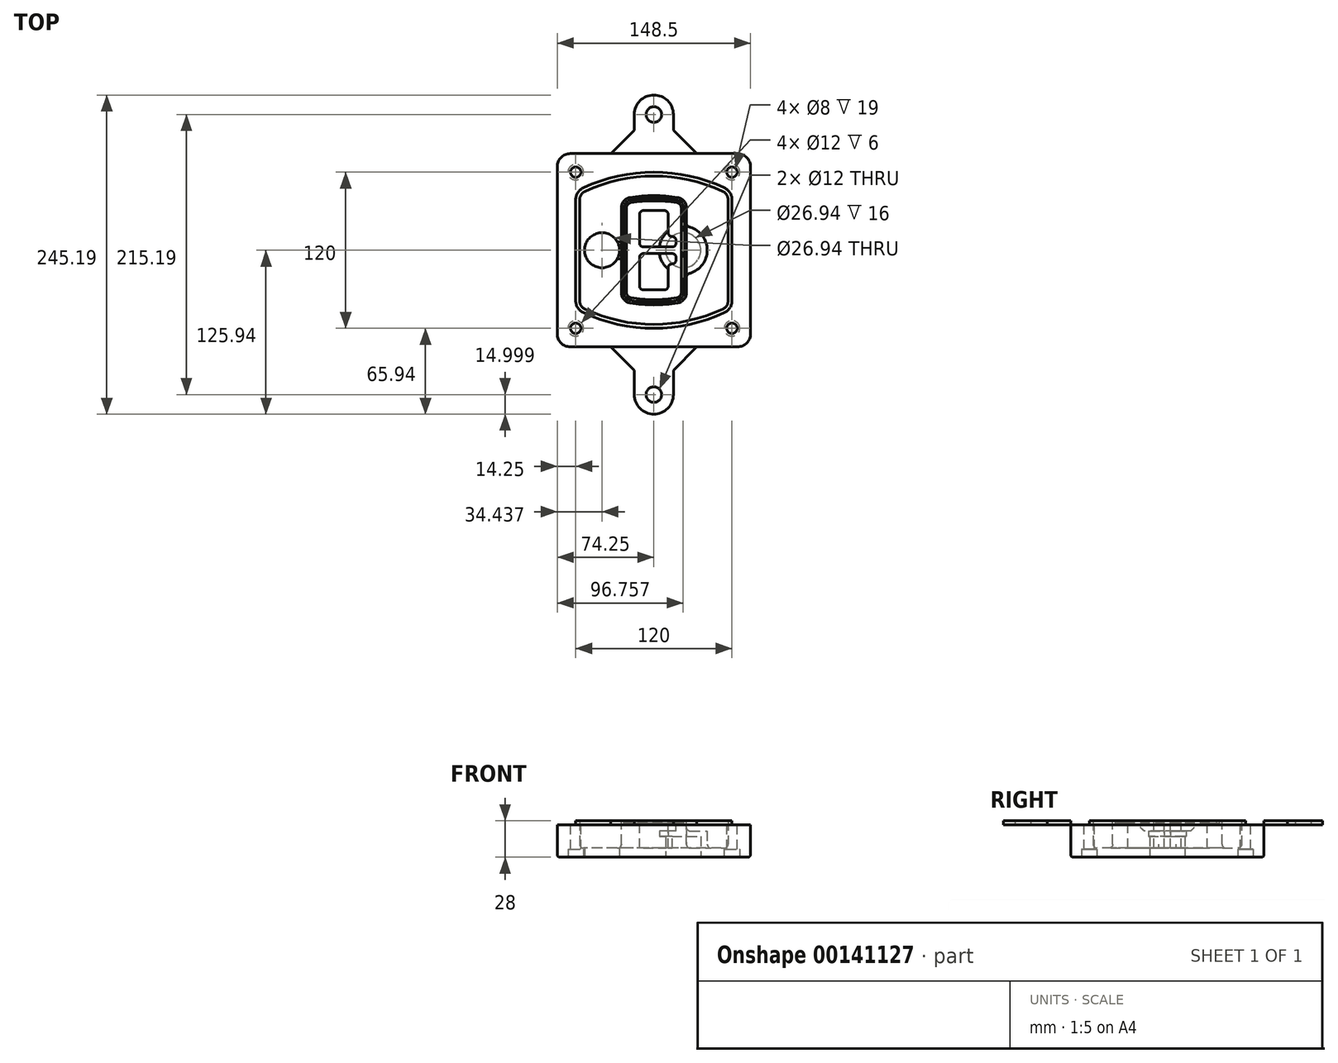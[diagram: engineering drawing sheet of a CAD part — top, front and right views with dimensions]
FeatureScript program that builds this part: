
annotation { "Feature Type Name" : "Feature", "Feature Type Description" : "" }
export const myFeature = defineFeature(function(context is Context, id is Id, definition is map)
    precondition{}
    {
        {
            var Q0;
            Q0=qCreatedBy(makeId("Top.planeOp"),FACE);
            var sketch = newSketch(context, id + "F0", { "sketchPlane" : qUnion([Q0])});
            skPoint(sketch, "E0.rect.middle", {"position": v(0, 0) * mm});
            skLineSegment(sketch, "E1.bottom", {"start": v(-64.25, -74.25) * mm, "end": v(64.25, -74.25) * mm});
            skLineSegment(sketch, "E1.top", {"start": v(-64.25, 74.25) * mm, "end": v(64.25, 74.25) * mm});
            skLineSegment(sketch, "E1.left", {"start": v(-74.25, -64.25) * mm, "end": v(-74.25, 64.25) * mm});
            skLineSegment(sketch, "E1.right", {"start": v(74.25, -64.25) * mm, "end": v(74.25, 64.25) * mm});
            skLineSegment(sketch, "E2", {"start": v(-74.25, 74.25) * mm, "end": v(74.25, -74.25) * mm, "construction": true});
            skLineSegment(sketch, "E3", {"start": v(74.25, 74.25) * mm, "end": v(-74.25, -74.25) * mm, "construction": true});
            skCircle(sketch, "E4", {"center": v(-60, 60) * mm, "radius": 4 * mm});
            skCircle(sketch, "E5", {"center": v(60, 60) * mm, "radius": 4 * mm});
            skCircle(sketch, "E6", {"center": v(60, -60) * mm, "radius": 4 * mm});
            skCircle(sketch, "E7", {"center": v(-60, -60) * mm, "radius": 4 * mm});
            skLineSegment(sketch, "E8", {"start": v(-60, 60) * mm, "end": v(60, 60) * mm, "construction": true});
            skLineSegment(sketch, "E9", {"start": v(60, 60) * mm, "end": v(60, -60) * mm, "construction": true});
            skLineSegment(sketch, "E10", {"start": v(60, -60) * mm, "end": v(-60, -60) * mm, "construction": true});
            skLineSegment(sketch, "E11", {"start": v(-60, -60) * mm, "end": v(-60, 60) * mm, "construction": true});
            skLineSegment(sketch, "E12", {"start": v(-60, 38.83) * mm, "end": v(-60, -38.83) * mm});
            skLineSegment(sketch, "E13", {"start": v(60, 38.83) * mm, "end": v(60, -38.83) * mm});
            skArc(sketch, "E14", {"start": v(54.26, 47.88) * mm, "mid": v(0, 60) * mm, "end": v(-54.26, 47.88) * mm});
            skArc(sketch, "E15", {"start": v(-54.26, -47.88) * mm, "mid": v(0, -60) * mm, "end": v(54.26, -47.88) * mm});
            skLineSegment(sketch, "E16", {"start": v(-60, 0) * mm, "end": v(60, 0) * mm, "construction": true});
            skPoint(sketch, "E17.visualSharp", {"position": v(-60, -45) * mm});
            skArc(sketch, "E17.filletArc", {"start": v(-60, -38.83) * mm, "mid": v(-58.44, -44.2) * mm, "end": v(-54.26, -47.88) * mm});
            skPoint(sketch, "E18.visualSharp", {"position": v(-60, 45) * mm});
            skArc(sketch, "E18.filletArc", {"start": v(-54.26, 47.88) * mm, "mid": v(-58.44, 44.2) * mm, "end": v(-60, 38.83) * mm});
            skPoint(sketch, "E19.visualSharp", {"position": v(60, 45) * mm});
            skArc(sketch, "E19.filletArc", {"start": v(60, 38.83) * mm, "mid": v(58.44, 44.2) * mm, "end": v(54.26, 47.88) * mm});
            skPoint(sketch, "E20.visualSharp", {"position": v(60, -45) * mm});
            skArc(sketch, "E20.filletArc", {"start": v(54.26, -47.88) * mm, "mid": v(58.44, -44.2) * mm, "end": v(60, -38.83) * mm});
            skPoint(sketch, "E21.visualSharp", {"position": v(-74.25, 74.25) * mm});
            skArc(sketch, "E21.filletArc", {"start": v(-64.25, 74.25) * mm, "mid": v(-71.32, 71.32) * mm, "end": v(-74.25, 64.25) * mm});
            skPoint(sketch, "E22.visualSharp", {"position": v(74.25, 74.25) * mm});
            skArc(sketch, "E22.filletArc", {"start": v(74.25, 64.25) * mm, "mid": v(71.32, 71.32) * mm, "end": v(64.25, 74.25) * mm});
            skPoint(sketch, "E23.visualSharp", {"position": v(74.25, -74.25) * mm});
            skArc(sketch, "E23.filletArc", {"start": v(64.25, -74.25) * mm, "mid": v(71.32, -71.32) * mm, "end": v(74.25, -64.25) * mm});
            skPoint(sketch, "E24.visualSharp", {"position": v(-74.25, -74.25) * mm});
            skArc(sketch, "E24.filletArc", {"start": v(-74.25, -64.25) * mm, "mid": v(-71.32, -71.32) * mm, "end": v(-64.25, -74.25) * mm});
            skArc(sketch, "E25.0", {"start": v(57, 38.83) * mm, "mid": v(55.9, 42.58) * mm, "end": v(52.98, 45.17) * mm});
            skLineSegment(sketch, "E25.1", {"start": v(57, 38.83) * mm, "end": v(57, -38.83) * mm});
            skArc(sketch, "E25.2", {"start": v(52.98, -45.17) * mm, "mid": v(55.9, -42.58) * mm, "end": v(57, -38.83) * mm});
            skArc(sketch, "E25.3", {"start": v(-52.98, -45.17) * mm, "mid": v(0, -57) * mm, "end": v(52.98, -45.17) * mm});
            skArc(sketch, "E25.4", {"start": v(-57, -38.83) * mm, "mid": v(-55.9, -42.58) * mm, "end": v(-52.98, -45.17) * mm});
            skArc(sketch, "E25.5", {"start": v(52.98, 45.17) * mm, "mid": v(0, 57) * mm, "end": v(-52.98, 45.17) * mm});
            skLineSegment(sketch, "E25.6", {"start": v(-57, 38.83) * mm, "end": v(-57, -38.83) * mm});
            skArc(sketch, "E25.7", {"start": v(-52.98, 45.17) * mm, "mid": v(-55.9, 42.58) * mm, "end": v(-57, 38.83) * mm});
            skArc(sketch, "E26.0", {"start": v(-55.96, 51.5) * mm, "mid": v(-61.82, 46.33) * mm, "end": v(-64, 38.83) * mm});
            skArc(sketch, "E26.1", {"start": v(55.96, 51.5) * mm, "mid": v(0, 64) * mm, "end": v(-55.96, 51.5) * mm});
            skArc(sketch, "E26.2", {"start": v(64, 38.83) * mm, "mid": v(61.82, 46.33) * mm, "end": v(55.96, 51.5) * mm});
            skLineSegment(sketch, "E26.3", {"start": v(64, 38.83) * mm, "end": v(64, -38.83) * mm});
            skArc(sketch, "E26.4", {"start": v(55.96, -51.5) * mm, "mid": v(61.82, -46.33) * mm, "end": v(64, -38.83) * mm});
            skLineSegment(sketch, "E26.5", {"start": v(-64, 38.83) * mm, "end": v(-64, -38.83) * mm});
            skArc(sketch, "E26.6", {"start": v(-55.96, -51.5) * mm, "mid": v(0, -64) * mm, "end": v(55.96, -51.5) * mm});
            skArc(sketch, "E26.7", {"start": v(-64, -38.83) * mm, "mid": v(-61.82, -46.33) * mm, "end": v(-55.96, -51.5) * mm});
            skSolve(sketch);
        }
        {
            var Q0;
            Q0=makeQuery(id+"F0.imprint","IMPRINT",FACE,{"disambiguationData":[TD([[makeQuery(id+"F0.imprint","IMPRINT",EDGE,{"derivedFrom":sQuery(id+"F0.wireOp",EDGE,"E1.bottom")}),1.0]])]});
            var Q1;
            Q1=makeQuery(id+"F0.imprint","IMPRINT",FACE,{"disambiguationData":[TD([[makeQuery(id+"F0.imprint","IMPRINT",EDGE,{"derivedFrom":sQuery(id+"F0.wireOp",EDGE,"E12")}),1.0]])]});
            var Q2;
            Q2=makeQuery(id+"F0.imprint","IMPRINT",FACE,{"disambiguationData":[TD([[makeQuery(id+"F0.imprint","IMPRINT",EDGE,{"derivedFrom":sQuery(id+"F0.wireOp",EDGE,"E25.0")}),1.0]])]});
            var Q3;
            Q3=makeQuery(id+"F0.imprint","IMPRINT",FACE,{"disambiguationData":[TD([[makeQuery(id+"F0.imprint","IMPRINT",EDGE,{"derivedFrom":sQuery(id+"F0.wireOp",EDGE,"E12")}),-1.0]])]});
            extrude(context, id + "F1", {"entities" : qUnion([Q0, Q1, Q2, Q3]), "oppositeDirection" : true, "depth" : 25 * mm});
        }
        {
            var Q0;
            Q0=makeQuery(id+"F0.imprint","IMPRINT",FACE,{"disambiguationData":[TD([[makeQuery(id+"F0.imprint","IMPRINT",EDGE,{"derivedFrom":sQuery(id+"F0.wireOp",EDGE,"E12")}),1.0]])]});
            extrude(context, id + "F2", {"entities" : qUnion([Q0]), "operationType" : NewBodyOperationType.ADD, "depth" : 3 * mm});
        }
        {
            var Q0;
            Q0=makeQuery(id+"F0.imprint","IMPRINT",FACE,{"disambiguationData":[TD([[makeQuery(id+"F0.imprint","IMPRINT",EDGE,{"derivedFrom":sQuery(id+"F0.wireOp",EDGE,"E25.0")}),1.0]])]});
            extrude(context, id + "F3", {"entities" : qUnion([Q0]), "operationType" : NewBodyOperationType.REMOVE, "oppositeDirection" : true, "depth" : 18 * mm});
        }
        {
            var Q0;
            Q0=makeQuery(id+"F2.opExtrude","CAP_FACE",FACE,{"disambiguationData":[OSD([sQuery(id+"F0.wireOp",EDGE,"E12"),sQuery(id+"F0.wireOp",EDGE,"E13"),sQuery(id+"F0.wireOp",EDGE,"E14"),sQuery(id+"F0.wireOp",EDGE,"E15"),sQuery(id+"F0.wireOp",EDGE,"E17.filletArc"),sQuery(id+"F0.wireOp",EDGE,"E18.filletArc"),sQuery(id+"F0.wireOp",EDGE,"E19.filletArc"),sQuery(id+"F0.wireOp",EDGE,"E20.filletArc"),sQuery(id+"F0.wireOp",EDGE,"E25.0"),sQuery(id+"F0.wireOp",EDGE,"E25.1"),sQuery(id+"F0.wireOp",EDGE,"E25.2"),sQuery(id+"F0.wireOp",EDGE,"E25.3"),sQuery(id+"F0.wireOp",EDGE,"E25.4"),sQuery(id+"F0.wireOp",EDGE,"E25.5"),sQuery(id+"F0.wireOp",EDGE,"E25.6"),sQuery(id+"F0.wireOp",EDGE,"E25.7")])],"isStart":false});
            var sketch = newSketch(context, id + "F4", { "sketchPlane" : qUnion([Q0])});
            skArc(sketch, "E27.0", {"start": v(-18.34, -40.45) * mm, "mid": v(0, -42) * mm, "end": v(18.34, -40.45) * mm});
            skArc(sketch, "E28.0", {"start": v(18.34, 40.45) * mm, "mid": v(0, 42) * mm, "end": v(-18.34, 40.45) * mm});
            skLineSegment(sketch, "E29", {"start": v(-25, 32.57) * mm, "end": v(-25, -32.57) * mm});
            skLineSegment(sketch, "E30", {"start": v(25, 32.57) * mm, "end": v(25, -32.57) * mm});
            skLineSegment(sketch, "E31", {"start": v(-25, 39.1) * mm, "end": v(25, 39.1) * mm, "construction": true});
            skLineSegment(sketch, "E32", {"start": v(-25, -39.1) * mm, "end": v(25, -39.1) * mm, "construction": true});
            skPoint(sketch, "E33.visualSharp", {"position": v(-25, 39.1) * mm});
            skArc(sketch, "E33.filletArc", {"start": v(-18.34, 40.45) * mm, "mid": v(-23.11, 37.73) * mm, "end": v(-25, 32.57) * mm});
            skPoint(sketch, "E34.visualSharp", {"position": v(25, 39.1) * mm});
            skArc(sketch, "E34.filletArc", {"start": v(25, 32.57) * mm, "mid": v(23.11, 37.73) * mm, "end": v(18.34, 40.45) * mm});
            skPoint(sketch, "E35.visualSharp", {"position": v(25, -39.1) * mm});
            skArc(sketch, "E35.filletArc", {"start": v(18.34, -40.45) * mm, "mid": v(23.11, -37.73) * mm, "end": v(25, -32.57) * mm});
            skPoint(sketch, "E36.visualSharp", {"position": v(-25, -39.1) * mm});
            skArc(sketch, "E36.filletArc", {"start": v(-25, -32.57) * mm, "mid": v(-23.11, -37.73) * mm, "end": v(-18.34, -40.45) * mm});
            skArc(sketch, "E37.0", {"start": v(52.98, 45.17) * mm, "mid": v(0, 57) * mm, "end": v(-52.98, 45.17) * mm});
            skArc(sketch, "E37.1", {"start": v(-52.98, 45.17) * mm, "mid": v(-55.9, 42.58) * mm, "end": v(-57, 38.83) * mm});
            skLineSegment(sketch, "E37.2", {"start": v(-57, 38.83) * mm, "end": v(-57, -38.83) * mm});
            skArc(sketch, "E37.3", {"start": v(-57, -38.83) * mm, "mid": v(-55.9, -42.58) * mm, "end": v(-52.98, -45.17) * mm});
            skArc(sketch, "E37.4", {"start": v(-52.98, -45.17) * mm, "mid": v(0, -57) * mm, "end": v(52.98, -45.17) * mm});
            skArc(sketch, "E37.5", {"start": v(52.98, -45.17) * mm, "mid": v(55.9, -42.58) * mm, "end": v(57, -38.83) * mm});
            skLineSegment(sketch, "E37.6", {"start": v(57, 38.83) * mm, "end": v(57, -38.83) * mm});
            skArc(sketch, "E37.7", {"start": v(57, 38.83) * mm, "mid": v(55.9, 42.58) * mm, "end": v(52.98, 45.17) * mm});
            skLineSegment(sketch, "E38.0", {"start": v(23, 32.57) * mm, "end": v(23, -32.57) * mm});
            skArc(sketch, "E38.1", {"start": v(18, -38.48) * mm, "mid": v(21.58, -36.44) * mm, "end": v(23, -32.57) * mm});
            skArc(sketch, "E38.2", {"start": v(-18, -38.48) * mm, "mid": v(0, -40) * mm, "end": v(18, -38.48) * mm});
            skArc(sketch, "E38.3", {"start": v(-23, -32.57) * mm, "mid": v(-21.58, -36.44) * mm, "end": v(-18, -38.48) * mm});
            skLineSegment(sketch, "E38.4", {"start": v(-23, 32.57) * mm, "end": v(-23, -32.57) * mm});
            skArc(sketch, "E38.5", {"start": v(23, 32.57) * mm, "mid": v(21.58, 36.44) * mm, "end": v(18, 38.48) * mm});
            skArc(sketch, "E38.6", {"start": v(-18, 38.48) * mm, "mid": v(-21.58, 36.44) * mm, "end": v(-23, 32.57) * mm});
            skArc(sketch, "E38.7", {"start": v(18, 38.48) * mm, "mid": v(0, 40) * mm, "end": v(-18, 38.48) * mm});
            skArc(sketch, "E39.0", {"start": v(21, 32.57) * mm, "mid": v(20.06, 35.15) * mm, "end": v(17.67, 36.5) * mm});
            skLineSegment(sketch, "E39.1", {"start": v(21, 32.57) * mm, "end": v(21, -32.57) * mm});
            skArc(sketch, "E39.2", {"start": v(17.67, -36.5) * mm, "mid": v(20.06, -35.15) * mm, "end": v(21, -32.57) * mm});
            skArc(sketch, "E39.3", {"start": v(-17.67, -36.5) * mm, "mid": v(0, -38) * mm, "end": v(17.67, -36.5) * mm});
            skArc(sketch, "E39.4", {"start": v(-21, -32.57) * mm, "mid": v(-20.06, -35.15) * mm, "end": v(-17.67, -36.5) * mm});
            skArc(sketch, "E39.5", {"start": v(17.67, 36.5) * mm, "mid": v(0, 38) * mm, "end": v(-17.67, 36.5) * mm});
            skLineSegment(sketch, "E39.6", {"start": v(-21, 32.57) * mm, "end": v(-21, -32.57) * mm});
            skArc(sketch, "E39.7", {"start": v(-17.67, 36.5) * mm, "mid": v(-20.06, 35.15) * mm, "end": v(-21, 32.57) * mm});
            skLineSegment(sketch, "E40", {"start": v(-25, 0) * mm, "end": v(25, 0) * mm, "construction": true});
            skLineSegment(sketch, "E41", {"start": v(-11, 5.5) * mm, "end": v(-11, 27.5) * mm});
            skLineSegment(sketch, "E42", {"start": v(-8, 30.5) * mm, "end": v(8, 30.5) * mm});
            skLineSegment(sketch, "E43", {"start": v(11, 27.5) * mm, "end": v(11, 13.5) * mm});
            skLineSegment(sketch, "E44", {"start": v(14, 10.5) * mm, "end": v(14, 10.5) * mm});
            skLineSegment(sketch, "E45", {"start": v(17, 7.5) * mm, "end": v(17, 5.5) * mm});
            skLineSegment(sketch, "E46", {"start": v(14, 2.5) * mm, "end": v(-8, 2.5) * mm});
            skPoint(sketch, "E47.visualSharp", {"position": v(-11, 30.5) * mm});
            skArc(sketch, "E47.filletArc", {"start": v(-8, 30.5) * mm, "mid": v(-10.12, 29.62) * mm, "end": v(-11, 27.5) * mm});
            skPoint(sketch, "E48.visualSharp", {"position": v(11, 30.5) * mm});
            skArc(sketch, "E48.filletArc", {"start": v(11, 27.5) * mm, "mid": v(10.12, 29.62) * mm, "end": v(8, 30.5) * mm});
            skPoint(sketch, "E49.visualSharp", {"position": v(11, 10.5) * mm});
            skArc(sketch, "E49.filletArc", {"start": v(11, 13.5) * mm, "mid": v(11.88, 11.38) * mm, "end": v(14, 10.5) * mm});
            skPoint(sketch, "E50.visualSharp", {"position": v(17, 10.5) * mm});
            skArc(sketch, "E50.filletArc", {"start": v(17, 7.5) * mm, "mid": v(16.12, 9.62) * mm, "end": v(14, 10.5) * mm});
            skPoint(sketch, "E51.visualSharp", {"position": v(17, 2.5) * mm});
            skArc(sketch, "E51.filletArc", {"start": v(14, 2.5) * mm, "mid": v(16.12, 3.38) * mm, "end": v(17, 5.5) * mm});
            skPoint(sketch, "E52.visualSharp", {"position": v(-11, 2.5) * mm});
            skArc(sketch, "E52.filletArc", {"start": v(-11, 5.5) * mm, "mid": v(-10.12, 3.38) * mm, "end": v(-8, 2.5) * mm});
            skLineSegment(sketch, "E53.0.MirrorCS", {"start": v(14, -2.5) * mm, "end": v(-8, -2.5) * mm});
            skArc(sketch, "E54.0.MirrorCS", {"start": v(-11, -5.5) * mm, "mid": v(-10.12, -3.38) * mm, "end": v(-8, -2.5) * mm});
            skLineSegment(sketch, "E55.0.MirrorCS", {"start": v(-11, -5.5) * mm, "end": v(-11, -27.5) * mm});
            skArc(sketch, "E56.0.MirrorCS", {"start": v(-8, -30.5) * mm, "mid": v(-10.12, -29.62) * mm, "end": v(-11, -27.5) * mm});
            skLineSegment(sketch, "E57.0.MirrorCS", {"start": v(-8, -30.5) * mm, "end": v(8, -30.5) * mm});
            skArc(sketch, "E58.0.MirrorCS", {"start": v(11, -27.5) * mm, "mid": v(10.12, -29.62) * mm, "end": v(8, -30.5) * mm});
            skLineSegment(sketch, "E59.0.MirrorCS", {"start": v(11, -27.5) * mm, "end": v(11, -13.5) * mm});
            skArc(sketch, "E60.0.MirrorCS", {"start": v(11, -13.5) * mm, "mid": v(11.88, -11.38) * mm, "end": v(14, -10.5) * mm});
            skArc(sketch, "E61.0.MirrorCS", {"start": v(17, -7.5) * mm, "mid": v(16.12, -9.62) * mm, "end": v(14, -10.5) * mm});
            skLineSegment(sketch, "E62.0.MirrorCS", {"start": v(17, -7.5) * mm, "end": v(17, -5.5) * mm});
            skArc(sketch, "E63.0.MirrorCS", {"start": v(14, -2.5) * mm, "mid": v(16.12, -3.38) * mm, "end": v(17, -5.5) * mm});
            skSolve(sketch);
        }
        {
            var Q0;
            Q0=makeQuery(id+"F4.imprint","IMPRINT",FACE,{"disambiguationData":[TD([[makeQuery(id+"F4.imprint","IMPRINT",EDGE,{"derivedFrom":sQuery(id+"F4.wireOp",EDGE,"E27.0")}),1.0]])]});
            var Q1;
            Q1=makeQuery(id+"F4.imprint","IMPRINT",FACE,{"disambiguationData":[TD([[makeQuery(id+"F4.imprint","IMPRINT",EDGE,{"derivedFrom":sQuery(id+"F4.wireOp",EDGE,"E38.0")}),-1.0]])]});
            var Q2;
            Q2=makeQuery(id+"F4.imprint","IMPRINT",FACE,{"disambiguationData":[TD([[makeQuery(id+"F4.imprint","IMPRINT",EDGE,{"derivedFrom":sQuery(id+"F4.wireOp",EDGE,"E39.0")}),1.0]])]});
            extrude(context, id + "F5", {"entities" : qUnion([Q0, Q1, Q2]), "operationType" : NewBodyOperationType.ADD, "endBound" : BoundingType.UP_TO_NEXT, "oppositeDirection" : true, "depth" : 25 * mm});
        }
        {
            var Q0;
            Q0=makeQuery(id+"F4.imprint","IMPRINT",FACE,{"disambiguationData":[TD([[makeQuery(id+"F4.imprint","IMPRINT",EDGE,{"derivedFrom":sQuery(id+"F4.wireOp",EDGE,"E38.0")}),-1.0]])]});
            extrude(context, id + "F6", {"entities" : qUnion([Q0]), "operationType" : NewBodyOperationType.REMOVE, "oppositeDirection" : true, "depth" : 2 * mm});
        }
        {
            var Q0;
            Q0=makeQuery(id+"F1.opExtrude","CAP_FACE",FACE,{"disambiguationData":[OSD([sQuery(id+"F0.wireOp",EDGE,"E1.bottom"),sQuery(id+"F0.wireOp",EDGE,"E1.top"),sQuery(id+"F0.wireOp",EDGE,"E1.left"),sQuery(id+"F0.wireOp",EDGE,"E1.right"),sQuery(id+"F0.wireOp",EDGE,"E4"),sQuery(id+"F0.wireOp",EDGE,"E5"),sQuery(id+"F0.wireOp",EDGE,"E6"),sQuery(id+"F0.wireOp",EDGE,"E7"),sQuery(id+"F0.wireOp",EDGE,"E21.filletArc"),sQuery(id+"F0.wireOp",EDGE,"E22.filletArc"),sQuery(id+"F0.wireOp",EDGE,"E23.filletArc"),sQuery(id+"F0.wireOp",EDGE,"E24.filletArc")])],"isStart":false});
            var sketch = newSketch(context, id + "F7", { "sketchPlane" : qUnion([Q0])});
            skCircle(sketch, "E64", {"center": v(22.5, 0) * mm, "radius": 13.47 * mm});
            skCircle(sketch, "E65", {"center": v(-39.81, 0) * mm, "radius": 13.47 * mm});
            skLineSegment(sketch, "E66", {"start": v(74.25, 0) * mm, "end": v(-74.25, 0) * mm});
            skCircle(sketch, "E67", {"center": v(22.5, 0) * mm, "radius": 18.47 * mm});
            skCircle(sketch, "E68", {"center": v(60, -60) * mm, "radius": 6 * mm});
            skCircle(sketch, "E69", {"center": v(-60, -60) * mm, "radius": 6 * mm});
            skCircle(sketch, "E70", {"center": v(-60, 60) * mm, "radius": 6 * mm});
            skCircle(sketch, "E71", {"center": v(60, 60) * mm, "radius": 6 * mm});
            skSolve(sketch);
        }
        {
            var Q0;
            {var subQ1=sQuery(id+"F7.wireOp",EDGE,"E66");var subQ4=sQuery(id+"F7.wireOp",EDGE,"E64");var subQ6=makeQuery(id+"F7.imprint","INTERSECT",VERTEX,{"disambiguationData":[OD(0.0)],"derivedFrom":[subQ4,subQ1]});Q0=makeQuery(id+"F7.imprint","IMPRINT",FACE,{"disambiguationData":[TD([[makeQuery(id+"F7.imprint","IMPRINT",EDGE,{"disambiguationData":[TD([[subQ6,-1.0]])],"derivedFrom":subQ4}),-1.0]])]});}
            var Q1;
            {var subQ0=sQuery(id+"F7.wireOp",EDGE,"E66");var subQ1=sQuery(id+"F7.wireOp",EDGE,"E64");var subQ3=makeQuery(id+"F7.imprint","INTERSECT",VERTEX,{"disambiguationData":[OD(0.0)],"derivedFrom":[subQ1,subQ0]});Q1=makeQuery(id+"F7.imprint","IMPRINT",FACE,{"disambiguationData":[TD([[makeQuery(id+"F7.imprint","IMPRINT",EDGE,{"disambiguationData":[TD([[subQ3,-1.0]])],"derivedFrom":subQ1}),1.0]])]});}
            var Q2;
            {var subQ0=sQuery(id+"F7.wireOp",EDGE,"E66");var subQ1=sQuery(id+"F7.wireOp",EDGE,"E64");var subQ3=makeQuery(id+"F7.imprint","INTERSECT",VERTEX,{"disambiguationData":[OD(0.0)],"derivedFrom":[subQ1,subQ0]});Q2=makeQuery(id+"F7.imprint","IMPRINT",FACE,{"disambiguationData":[TD([[makeQuery(id+"F7.imprint","IMPRINT",EDGE,{"disambiguationData":[TD([[subQ3,1.0]])],"derivedFrom":subQ1}),1.0]])]});}
            var Q3;
            {var subQ1=sQuery(id+"F7.wireOp",EDGE,"E66");var subQ4=sQuery(id+"F7.wireOp",EDGE,"E64");var subQ6=makeQuery(id+"F7.imprint","INTERSECT",VERTEX,{"disambiguationData":[OD(0.0)],"derivedFrom":[subQ4,subQ1]});Q3=makeQuery(id+"F7.imprint","IMPRINT",FACE,{"disambiguationData":[TD([[makeQuery(id+"F7.imprint","IMPRINT",EDGE,{"disambiguationData":[TD([[subQ6,1.0]])],"derivedFrom":subQ4}),-1.0]])]});}
            extrude(context, id + "F8", {"entities" : qUnion([Q0, Q1, Q2, Q3]), "operationType" : NewBodyOperationType.ADD, "oppositeDirection" : true, "depth" : 20 * mm});
        }
        {
            var Q0;
            {var subQ0=sQuery(id+"F7.wireOp",EDGE,"E66");var subQ1=sQuery(id+"F7.wireOp",EDGE,"E64");var subQ3=makeQuery(id+"F7.imprint","INTERSECT",VERTEX,{"disambiguationData":[OD(0.0)],"derivedFrom":[subQ1,subQ0]});Q0=makeQuery(id+"F7.imprint","IMPRINT",FACE,{"disambiguationData":[TD([[makeQuery(id+"F7.imprint","IMPRINT",EDGE,{"disambiguationData":[TD([[subQ3,-1.0]])],"derivedFrom":subQ1}),1.0]])]});}
            var Q1;
            {var subQ0=sQuery(id+"F7.wireOp",EDGE,"E66");var subQ1=sQuery(id+"F7.wireOp",EDGE,"E64");var subQ3=makeQuery(id+"F7.imprint","INTERSECT",VERTEX,{"disambiguationData":[OD(0.0)],"derivedFrom":[subQ1,subQ0]});Q1=makeQuery(id+"F7.imprint","IMPRINT",FACE,{"disambiguationData":[TD([[makeQuery(id+"F7.imprint","IMPRINT",EDGE,{"disambiguationData":[TD([[subQ3,1.0]])],"derivedFrom":subQ1}),1.0]])]});}
            extrude(context, id + "F9", {"entities" : qUnion([Q0, Q1]), "operationType" : NewBodyOperationType.REMOVE, "oppositeDirection" : true, "depth" : 16 * mm});
        }
        {
            var Q0;
            {var subQ0=sQuery(id+"F7.wireOp",EDGE,"E66");var subQ1=sQuery(id+"F7.wireOp",EDGE,"E65");var subQ3=makeQuery(id+"F7.imprint","INTERSECT",VERTEX,{"disambiguationData":[OD(0.0)],"derivedFrom":[subQ1,subQ0]});Q0=makeQuery(id+"F7.imprint","IMPRINT",FACE,{"disambiguationData":[TD([[makeQuery(id+"F7.imprint","IMPRINT",EDGE,{"disambiguationData":[TD([[subQ3,-1.0]])],"derivedFrom":subQ1}),1.0]])]});}
            var Q1;
            {var subQ0=sQuery(id+"F7.wireOp",EDGE,"E66");var subQ1=sQuery(id+"F7.wireOp",EDGE,"E65");var subQ3=makeQuery(id+"F7.imprint","INTERSECT",VERTEX,{"disambiguationData":[OD(0.0)],"derivedFrom":[subQ1,subQ0]});Q1=makeQuery(id+"F7.imprint","IMPRINT",FACE,{"disambiguationData":[TD([[makeQuery(id+"F7.imprint","IMPRINT",EDGE,{"disambiguationData":[TD([[subQ3,1.0]])],"derivedFrom":subQ1}),1.0]])]});}
            extrude(context, id + "F10", {"entities" : qUnion([Q0, Q1]), "operationType" : NewBodyOperationType.REMOVE, "oppositeDirection" : true, "depth" : 25 * mm});
        }
        {
            var Q0;
            Q0=makeQuery(id+"F7.imprint","IMPRINT",FACE,{"disambiguationData":[TD([[makeQuery(id+"F7.imprint","IMPRINT",EDGE,{"derivedFrom":sQuery(id+"F7.wireOp",EDGE,"E68")}),1.0]])]});
            var Q1;
            Q1=makeQuery(id+"F7.imprint","IMPRINT",FACE,{"disambiguationData":[TD([[makeQuery(id+"F7.imprint","IMPRINT",EDGE,{"derivedFrom":makeQuery(id+"F1.opExtrude","CAP_EDGE",EDGE,{"disambiguationData":[OSD([sQuery(id+"F0.wireOp",EDGE,"E5")])],"isStart":false})}),-1.0]])]});
            var Q2;
            Q2=makeQuery(id+"F7.imprint","IMPRINT",FACE,{"disambiguationData":[TD([[makeQuery(id+"F7.imprint","IMPRINT",EDGE,{"derivedFrom":sQuery(id+"F7.wireOp",EDGE,"E69")}),1.0]])]});
            var Q3;
            Q3=makeQuery(id+"F7.imprint","IMPRINT",FACE,{"disambiguationData":[TD([[makeQuery(id+"F7.imprint","IMPRINT",EDGE,{"derivedFrom":makeQuery(id+"F1.opExtrude","CAP_EDGE",EDGE,{"disambiguationData":[OSD([sQuery(id+"F0.wireOp",EDGE,"E4")])],"isStart":false})}),-1.0]])]});
            var Q4;
            Q4=makeQuery(id+"F7.imprint","IMPRINT",FACE,{"disambiguationData":[TD([[makeQuery(id+"F7.imprint","IMPRINT",EDGE,{"derivedFrom":sQuery(id+"F7.wireOp",EDGE,"E70")}),1.0]])]});
            var Q5;
            Q5=makeQuery(id+"F7.imprint","IMPRINT",FACE,{"disambiguationData":[TD([[makeQuery(id+"F7.imprint","IMPRINT",EDGE,{"derivedFrom":makeQuery(id+"F1.opExtrude","CAP_EDGE",EDGE,{"disambiguationData":[OSD([sQuery(id+"F0.wireOp",EDGE,"E7")])],"isStart":false})}),-1.0]])]});
            var Q6;
            Q6=makeQuery(id+"F7.imprint","IMPRINT",FACE,{"disambiguationData":[TD([[makeQuery(id+"F7.imprint","IMPRINT",EDGE,{"derivedFrom":sQuery(id+"F7.wireOp",EDGE,"E71")}),1.0]])]});
            var Q7;
            Q7=makeQuery(id+"F7.imprint","IMPRINT",FACE,{"disambiguationData":[TD([[makeQuery(id+"F7.imprint","IMPRINT",EDGE,{"derivedFrom":makeQuery(id+"F1.opExtrude","CAP_EDGE",EDGE,{"disambiguationData":[OSD([sQuery(id+"F0.wireOp",EDGE,"E6")])],"isStart":false})}),-1.0]])]});
            extrude(context, id + "F11", {"entities" : qUnion([Q0, Q1, Q2, Q3, Q4, Q5, Q6, Q7]), "operationType" : NewBodyOperationType.REMOVE, "oppositeDirection" : true, "depth" : 6 * mm});
        }
        {
            var Q0;
            Q0=makeQuery(id+"F9.boolean.opBoolean","COPY",FACE,{"derivedFrom":makeQuery(id+"F9.opExtrude","CAP_FACE",FACE,{"disambiguationData":[OSD([sQuery(id+"F7.wireOp",EDGE,"E64")])],"isStart":false})});
            var sketch = newSketch(context, id + "F12", { "sketchPlane" : qUnion([Q0])});
            skArc(sketch, "E72.0", {"start": v(11, 14.45) * mm, "mid": v(6.45, 9.13) * mm, "end": v(4.2, 2.5) * mm});
            skArc(sketch, "E72.1", {"start": v(4.2, -2.5) * mm, "mid": v(6.45, -9.13) * mm, "end": v(11, -14.45) * mm});
            skLineSegment(sketch, "E73", {"start": v(4.2, -2.5) * mm, "end": v(14, -2.5) * mm});
            skLineSegment(sketch, "E74.0", {"start": v(14, 2.5) * mm, "end": v(4.2, 2.5) * mm});
            skArc(sketch, "E74.1", {"start": v(14, 2.5) * mm, "mid": v(16.12, 3.38) * mm, "end": v(17, 5.5) * mm});
            skLineSegment(sketch, "E74.2", {"start": v(17, 7.5) * mm, "end": v(17, 5.5) * mm});
            skArc(sketch, "E74.3", {"start": v(17, 7.5) * mm, "mid": v(16.12, 9.62) * mm, "end": v(14, 10.5) * mm});
            skArc(sketch, "E74.4", {"start": v(11, 13.5) * mm, "mid": v(11.88, 11.38) * mm, "end": v(14, 10.5) * mm});
            skLineSegment(sketch, "E74.5", {"start": v(11, 14.45) * mm, "end": v(11, 13.5) * mm});
            skLineSegment(sketch, "E74.7", {"start": v(14, -2.5) * mm, "end": v(4.2, -2.5) * mm});
            skArc(sketch, "E74.8", {"start": v(14, -2.5) * mm, "mid": v(16.12, -3.38) * mm, "end": v(17, -5.5) * mm});
            skLineSegment(sketch, "E74.9", {"start": v(17, -7.5) * mm, "end": v(17, -5.5) * mm});
            skArc(sketch, "E74.10", {"start": v(17, -7.5) * mm, "mid": v(16.12, -9.62) * mm, "end": v(14, -10.5) * mm});
            skArc(sketch, "E74.11", {"start": v(11, -13.5) * mm, "mid": v(11.88, -11.38) * mm, "end": v(14, -10.5) * mm});
            skLineSegment(sketch, "E74.12", {"start": v(11, -14.45) * mm, "end": v(11, -13.5) * mm});
            skPoint(sketch, "E75.orphan", {"position": v(11, -27.5) * mm});
            skPoint(sketch, "E76.orphan", {"position": v(-8, -2.5) * mm});
            skPoint(sketch, "E77.orphan", {"position": v(-8, 2.5) * mm});
            skPoint(sketch, "E78.orphan", {"position": v(11, 27.5) * mm});
            skSolve(sketch);
        }
        {
            var Q0;
            {var subQ7=sQuery(id+"F12.wireOp",EDGE,"E72.0");var subQ14=sQuery(id+"F12.wireOp",EDGE,"E72.1");var subQ16=sQuery(id+"F12.wireOp",EDGE,"E74.1");var subQ18=sQuery(id+"F12.wireOp",EDGE,"E74.8");Q0=qUnion([makeQuery(id+"F12.imprint","IMPRINT",FACE,{"disambiguationData":[TD([[makeQuery(id+"F12.imprint","IMPRINT",EDGE,{"derivedFrom":subQ7}),1.0]])]}),makeQuery(id+"F12.imprint","IMPRINT",FACE,{"disambiguationData":[TD([[makeQuery(id+"F12.imprint","IMPRINT",EDGE,{"derivedFrom":subQ14}),1.0]])]}),makeQuery(id+"F12.imprint","IMPRINT",FACE,{"disambiguationData":[TD([[makeQuery(id+"F12.imprint","IMPRINT",EDGE,{"derivedFrom":subQ16}),1.0]])]}),makeQuery(id+"F12.imprint","IMPRINT",FACE,{"disambiguationData":[TD([[makeQuery(id+"F12.imprint","IMPRINT",EDGE,{"derivedFrom":subQ18}),-1.0]])]})]);}
            var Q1;
            Q1=makeQuery(id+"F5.boolean.opBoolean","SPLIT",FACE,{"disambiguationData":[TD([makeQuery(id+"F5.opExtrude","SWEPT_FACE",FACE,{"disambiguationData":[OSD([sQuery(id+"F4.wireOp",EDGE,"E41")])]})])],"derivedFrom":makeQuery(id+"F3.boolean.opBoolean","COPY",FACE,{"derivedFrom":makeQuery(id+"F3.opExtrude","CAP_FACE",FACE,{"disambiguationData":[OSD([sQuery(id+"F0.wireOp",EDGE,"E25.0"),sQuery(id+"F0.wireOp",EDGE,"E25.1"),sQuery(id+"F0.wireOp",EDGE,"E25.2"),sQuery(id+"F0.wireOp",EDGE,"E25.3"),sQuery(id+"F0.wireOp",EDGE,"E25.4"),sQuery(id+"F0.wireOp",EDGE,"E25.5"),sQuery(id+"F0.wireOp",EDGE,"E25.6"),sQuery(id+"F0.wireOp",EDGE,"E25.7")])],"isStart":false})})});
            extrude(context, id + "F13", {"entities" : qUnion([Q0]), "operationType" : NewBodyOperationType.REMOVE, "endBound" : BoundingType.UP_TO_SURFACE, "endBoundEntityFace" : qUnion([Q1]), "depth" : 25 * mm});
        }
        {
            var Q0;
            Q0=makeQuery(id+"F3.boolean.opBoolean","COPY",EDGE,{"derivedFrom":makeQuery(id+"F3.opExtrude","CAP_EDGE",EDGE,{"disambiguationData":[OSD([sQuery(id+"F0.wireOp",EDGE,"E25.6")])],"isStart":false})});
            var Q1;
            Q1=makeQuery(id+"F8.boolean.opBoolean","INTERSECT",EDGE,{"derivedFrom":[makeQuery(id+"F5.opExtrude","SWEPT_FACE",FACE,{"disambiguationData":[OSD([sQuery(id+"F4.wireOp",EDGE,"E30")])]}),makeQuery(id+"F8.opExtrude","CAP_FACE",FACE,{"disambiguationData":[OSD([sQuery(id+"F7.wireOp",EDGE,"E67")])],"isStart":false})]});
            var Q2;
            Q2=makeQuery(id+"F8.boolean.opBoolean","INTERSECT",EDGE,{"disambiguationData":[OD(1.0)],"derivedFrom":[makeQuery(id+"F5.opExtrude","SWEPT_FACE",FACE,{"disambiguationData":[OSD([sQuery(id+"F4.wireOp",EDGE,"E30")])]}),makeQuery(id+"F8.opExtrude","SWEPT_FACE",FACE,{"disambiguationData":[OSD([sQuery(id+"F7.wireOp",EDGE,"E67")])]})]});
            var Q3;
            {var subQ0=sQuery(id+"F4.wireOp",EDGE,"E30");Q3=makeQuery(id+"F8.boolean.opBoolean","SPLIT",EDGE,{"disambiguationData":[TD([makeQuery(id+"F5.opExtrude","SWEPT_FACE",FACE,{"disambiguationData":[OSD([sQuery(id+"F4.wireOp",EDGE,"E35.filletArc")])]})])],"derivedFrom":makeQuery(id+"F5.opExtrude","CAP_EDGE",EDGE,{"disambiguationData":[OSD([subQ0])],"isStart":false})});}
            var Q4;
            {var subQ0=sQuery(id+"F0.wireOp",EDGE,"E25.7");var subQ1=sQuery(id+"F0.wireOp",EDGE,"E25.1");var subQ2=sQuery(id+"F0.wireOp",EDGE,"E25.6");var subQ3=sQuery(id+"F0.wireOp",EDGE,"E25.5");var subQ4=sQuery(id+"F0.wireOp",EDGE,"E25.4");var subQ5=sQuery(id+"F0.wireOp",EDGE,"E25.0");var subQ6=sQuery(id+"F0.wireOp",EDGE,"E25.2");var subQ7=sQuery(id+"F0.wireOp",EDGE,"E25.3");Q4=makeQuery(id+"F8.boolean.opBoolean","INTERSECT",EDGE,{"derivedFrom":[makeQuery(id+"F5.boolean.opBoolean","SPLIT",FACE,{"disambiguationData":[TD([makeQuery(id+"F2.opExtrude","SWEPT_FACE",FACE,{"disambiguationData":[OSD([subQ5])]})])],"derivedFrom":makeQuery(id+"F3.boolean.opBoolean","COPY",FACE,{"derivedFrom":makeQuery(id+"F3.opExtrude","CAP_FACE",FACE,{"disambiguationData":[OSD([subQ5,subQ1,subQ6,subQ7,subQ4,subQ3,subQ2,subQ0])],"isStart":false})})}),makeQuery(id+"F8.opExtrude","SWEPT_FACE",FACE,{"disambiguationData":[OSD([sQuery(id+"F7.wireOp",EDGE,"E67")])]})]});}
            var Q5;
            Q5=makeQuery(id+"F8.boolean.opBoolean","INTERSECT",EDGE,{"disambiguationData":[OD(0.0)],"derivedFrom":[makeQuery(id+"F5.opExtrude","SWEPT_FACE",FACE,{"disambiguationData":[OSD([sQuery(id+"F4.wireOp",EDGE,"E30")])]}),makeQuery(id+"F8.opExtrude","SWEPT_FACE",FACE,{"disambiguationData":[OSD([sQuery(id+"F7.wireOp",EDGE,"E67")])]})]});
            fillet(context, id + "F14", {"entities" : qUnion([Q0, Q1, Q2, Q3, Q4, Q5]), "radius" : 3 * mm, "tangentPropagation" : true, "allowEdgeOverflow" : false});
        }
        {
            var Q0;
            Q0=makeQuery(id+"F1.opExtrude","CAP_EDGE",EDGE,{"disambiguationData":[OSD([sQuery(id+"F0.wireOp",EDGE,"E1.bottom")])],"isStart":false});
            fillet(context, id + "F15", {"entities" : qUnion([Q0]), "radius" : 2 * mm, "tangentPropagation" : true, "allowEdgeOverflow" : false});
        }
        {
            var Q0;
            {var subQ0=sQuery(id+"F0.wireOp",EDGE,"E22.filletArc");var subQ1=sQuery(id+"F0.wireOp",EDGE,"E7");var subQ2=sQuery(id+"F0.wireOp",EDGE,"E6");var subQ3=sQuery(id+"F0.wireOp",EDGE,"E5");var subQ4=sQuery(id+"F0.wireOp",EDGE,"E4");var subQ5=sQuery(id+"F0.wireOp",EDGE,"E1.bottom");var subQ6=sQuery(id+"F0.wireOp",EDGE,"E21.filletArc");var subQ7=sQuery(id+"F0.wireOp",EDGE,"E1.top");var subQ8=sQuery(id+"F0.wireOp",EDGE,"E1.left");var subQ9=sQuery(id+"F0.wireOp",EDGE,"E1.right");var subQ10=sQuery(id+"F0.wireOp",EDGE,"E23.filletArc");var subQ11=sQuery(id+"F0.wireOp",EDGE,"E24.filletArc");Q0=makeQuery(id+"F2.boolean.opBoolean","SPLIT",FACE,{"disambiguationData":[TD([makeQuery(id+"F1.opExtrude","SWEPT_FACE",FACE,{"disambiguationData":[OSD([subQ5])]})])],"derivedFrom":makeQuery(id+"F1.opExtrude","CAP_FACE",FACE,{"disambiguationData":[OSD([subQ5,subQ7,subQ8,subQ9,subQ4,subQ3,subQ2,subQ1,subQ6,subQ0,subQ10,subQ11])],"isStart":true})});}
            var sketch = newSketch(context, id + "F16", { "sketchPlane" : qUnion([Q0])});
            skCircle(sketch, "E79", {"center": v(0, 104.25) * mm, "radius": 6 * mm});
            skPoint(sketch, "E79.centerSnap0", {"position": v(0, 74.25) * mm});
            skArc(sketch, "E80", {"start": v(-15, 104.25) * mm, "mid": v(0, 119.25) * mm, "end": v(15, 104.25) * mm});
            skLineSegment(sketch, "E81", {"start": v(-15, 104.25) * mm, "end": v(-15, 92.25) * mm});
            skLineSegment(sketch, "E82", {"start": v(15, 104.25) * mm, "end": v(15, 92.25) * mm});
            skLineSegment(sketch, "E83", {"start": v(15, 92.25) * mm, "end": v(33, 74.25) * mm});
            skLineSegment(sketch, "E84", {"start": v(-15, 92.25) * mm, "end": v(-32.84, 74.25) * mm});
            skCircle(sketch, "E85", {"center": v(0, -110.94) * mm, "radius": 6 * mm});
            skPoint(sketch, "E85.centerSnap0", {"position": v(0, -74.25) * mm});
            skArc(sketch, "E86", {"start": v(15, -110.94) * mm, "mid": v(0, -125.94) * mm, "end": v(-15, -110.94) * mm});
            skLineSegment(sketch, "E87", {"start": v(-15, -110.94) * mm, "end": v(-15, -92.25) * mm});
            skLineSegment(sketch, "E88", {"start": v(15, -110.94) * mm, "end": v(15, -92.25) * mm});
            skLineSegment(sketch, "E89", {"start": v(15, -92.25) * mm, "end": v(33, -74.25) * mm});
            skLineSegment(sketch, "E90", {"start": v(-15, -92.25) * mm, "end": v(-33, -74.25) * mm});
            skLineSegment(sketch, "E91", {"start": v(0, 104.25) * mm, "end": v(0, 74.25) * mm, "construction": true});
            skArc(sketch, "E92.MirrorCS", {"start": v(15, 104.25) * mm, "mid": v(0, 119.25) * mm, "end": v(-15, 104.25) * mm});
            skLineSegment(sketch, "E93.MirrorCS", {"start": v(15, 92.25) * mm, "end": v(32.84, 74.25) * mm});
            skLineSegment(sketch, "E94.MirrorCS", {"start": v(-15, 92.25) * mm, "end": v(-33, 74.25) * mm});
            skSolve(sketch);
        }
        {
            var Q0;
            {var subQ1=sQuery(id+"F16.wireOp",EDGE,"E84");Q0=makeQuery(id+"F16.imprint","IMPRINT",FACE,{"disambiguationData":[TD([[makeQuery(id+"F16.imprint","IMPRINT",EDGE,{"derivedFrom":subQ1}),1.0]])]});}
            var Q1;
            Q1=makeQuery(id+"F16.imprint","IMPRINT",FACE,{"disambiguationData":[TD([[makeQuery(id+"F16.imprint","IMPRINT",EDGE,{"derivedFrom":sQuery(id+"F16.wireOp",EDGE,"E85")}),-1.0]])]});
            var Q2;
            Q2=makeQuery(id+"F2.opExtrude","CAP_FACE",FACE,{"disambiguationData":[OSD([sQuery(id+"F0.wireOp",EDGE,"E12"),sQuery(id+"F0.wireOp",EDGE,"E13"),sQuery(id+"F0.wireOp",EDGE,"E14"),sQuery(id+"F0.wireOp",EDGE,"E15"),sQuery(id+"F0.wireOp",EDGE,"E17.filletArc"),sQuery(id+"F0.wireOp",EDGE,"E18.filletArc"),sQuery(id+"F0.wireOp",EDGE,"E19.filletArc"),sQuery(id+"F0.wireOp",EDGE,"E20.filletArc"),sQuery(id+"F0.wireOp",EDGE,"E25.0"),sQuery(id+"F0.wireOp",EDGE,"E25.1"),sQuery(id+"F0.wireOp",EDGE,"E25.2"),sQuery(id+"F0.wireOp",EDGE,"E25.3"),sQuery(id+"F0.wireOp",EDGE,"E25.4"),sQuery(id+"F0.wireOp",EDGE,"E25.5"),sQuery(id+"F0.wireOp",EDGE,"E25.6"),sQuery(id+"F0.wireOp",EDGE,"E25.7")])],"isStart":false});
            extrude(context, id + "F17", {"entities" : qUnion([Q0, Q1]), "endBound" : BoundingType.UP_TO_SURFACE, "endBoundEntityFace" : qUnion([Q2]), "depth" : 25 * mm});
        }
    });
